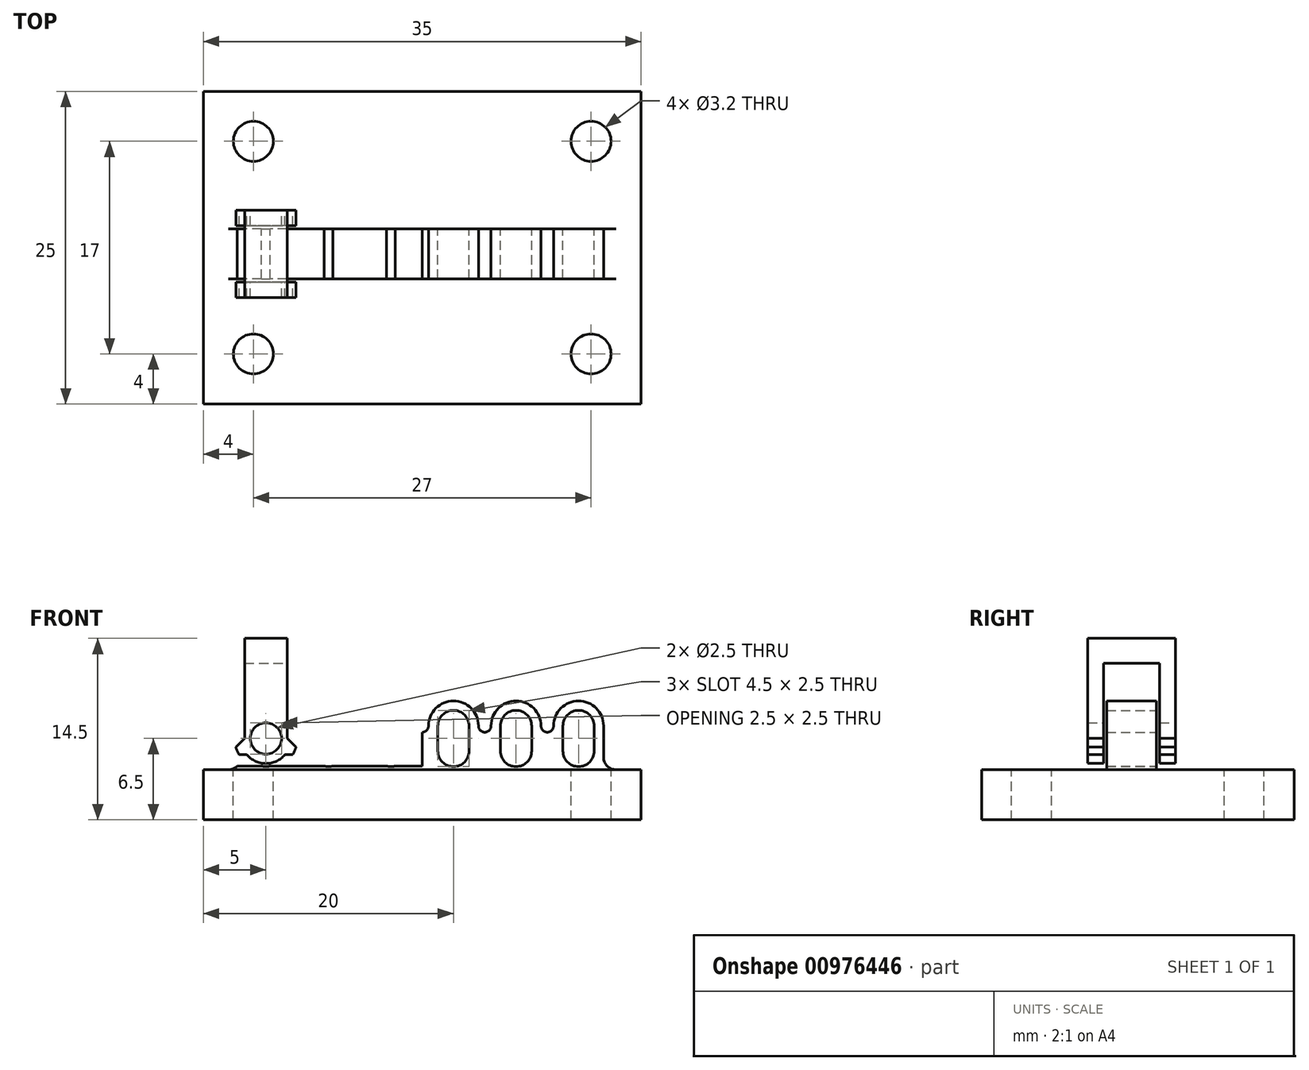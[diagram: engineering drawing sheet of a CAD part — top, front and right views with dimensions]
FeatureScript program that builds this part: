
annotation { "Feature Type Name" : "Feature", "Feature Type Description" : "" }
export const myFeature = defineFeature(function(context is Context, id is Id, definition is map)
    precondition{}
    {
        {
            var Q0;
            Q0=qCreatedBy(makeId("Front.planeOp"),FACE);
            var sketch = newSketch(context, id + "F0", { "sketchPlane" : qUnion([Q0])});
            skLineSegment(sketch, "E0.left", {"start": v(-1.25, 1) * mm, "end": v(-1.25, -1) * mm});
            skLineSegment(sketch, "E0.right", {"start": v(1.25, 1) * mm, "end": v(1.25, -1) * mm});
            skArc(sketch, "E1", {"start": v(1.25, 1) * mm, "mid": v(0, 2.25) * mm, "end": v(-1.25, 1) * mm});
            skArc(sketch, "E2", {"start": v(-1.25, -1) * mm, "mid": v(0, -2.25) * mm, "end": v(1.25, -1) * mm});
            skArc(sketch, "E3.1.0.0", {"start": v(3.75, -1) * mm, "mid": v(5, -2.25) * mm, "end": v(6.25, -1) * mm});
            skArc(sketch, "E3.1.0.1", {"start": v(6.25, 1) * mm, "mid": v(5, 2.25) * mm, "end": v(3.75, 1) * mm});
            skLineSegment(sketch, "E3.1.0.2", {"start": v(6.25, 1) * mm, "end": v(6.25, -1) * mm});
            skLineSegment(sketch, "E3.1.0.3", {"start": v(3.75, 1) * mm, "end": v(3.75, -1) * mm});
            skArc(sketch, "E3.2.0.0", {"start": v(8.75, -1) * mm, "mid": v(10, -2.25) * mm, "end": v(11.25, -1) * mm});
            skArc(sketch, "E3.2.0.1", {"start": v(11.25, 1) * mm, "mid": v(10, 2.25) * mm, "end": v(8.75, 1) * mm});
            skLineSegment(sketch, "E3.2.0.2", {"start": v(11.25, 1) * mm, "end": v(11.25, -1) * mm});
            skLineSegment(sketch, "E3.2.0.3", {"start": v(8.75, 1) * mm, "end": v(8.75, -1) * mm});
            skArc(sketch, "E3.3.0.0", {"start": v(13.75, -1) * mm, "mid": v(15, -2.25) * mm, "end": v(16.25, -1) * mm});
            skArc(sketch, "E3.3.0.1", {"start": v(16.25, 1) * mm, "mid": v(15, 2.25) * mm, "end": v(13.75, 1) * mm});
            skLineSegment(sketch, "E3.3.0.2", {"start": v(16.25, 1) * mm, "end": v(16.25, -1) * mm});
            skLineSegment(sketch, "E3.3.0.3", {"start": v(13.75, 1) * mm, "end": v(13.75, -1) * mm});
            skArc(sketch, "E3.4.0.0", {"start": v(18.75, -1) * mm, "mid": v(20, -2.25) * mm, "end": v(21.25, -1) * mm});
            skArc(sketch, "E3.4.0.1", {"start": v(21.25, 1) * mm, "mid": v(20, 2.25) * mm, "end": v(18.75, 1) * mm});
            skLineSegment(sketch, "E3.4.0.2", {"start": v(21.25, 1) * mm, "end": v(21.25, -1) * mm});
            skLineSegment(sketch, "E3.4.0.3", {"start": v(18.75, 1) * mm, "end": v(18.75, -1) * mm});
            skArc(sketch, "E3.5.0.0", {"start": v(23.75, -1) * mm, "mid": v(25, -2.25) * mm, "end": v(26.25, -1) * mm});
            skArc(sketch, "E3.5.0.1", {"start": v(26.25, 1) * mm, "mid": v(25, 2.25) * mm, "end": v(23.75, 1) * mm});
            skLineSegment(sketch, "E3.5.0.2", {"start": v(26.25, 1) * mm, "end": v(26.25, -1) * mm});
            skLineSegment(sketch, "E3.5.0.3", {"start": v(23.75, 1) * mm, "end": v(23.75, -1) * mm});
            skLineSegment(sketch, "E3.direction1", {"start": v(-1.25, -1) * mm, "end": v(3.75, -1) * mm, "construction": true});
            skLineSegment(sketch, "E4", {"start": v(-5, -6.5) * mm, "end": v(30, -6.5) * mm});
            skLineSegment(sketch, "E5", {"start": v(30, -6.5) * mm, "end": v(30, -2.5) * mm});
            skLineSegment(sketch, "E6", {"start": v(30, -2.5) * mm, "end": v(28, -2.5) * mm});
            skArc(sketch, "E7", {"start": v(27, -1.5) * mm, "mid": v(27.3, -2.2) * mm, "end": v(28, -2.5) * mm});
            skLineSegment(sketch, "E8", {"start": v(27, -1.5) * mm, "end": v(27, 1) * mm});
            skArc(sketch, "E9", {"start": v(27, 1) * mm, "mid": v(25, 3) * mm, "end": v(23, 1) * mm});
            skArc(sketch, "E10", {"start": v(22, 1) * mm, "mid": v(20, 3) * mm, "end": v(18, 1) * mm});
            skArc(sketch, "E11", {"start": v(17, 1) * mm, "mid": v(15, 3) * mm, "end": v(13, 1) * mm});
            skArc(sketch, "E12", {"start": v(12, 1) * mm, "mid": v(10, 3) * mm, "end": v(8, 1) * mm});
            skArc(sketch, "E13", {"start": v(7, 1) * mm, "mid": v(5, 3) * mm, "end": v(3, 1) * mm});
            skArc(sketch, "E14", {"start": v(2, 1) * mm, "mid": v(0, 3) * mm, "end": v(-2, 1) * mm});
            skLineSegment(sketch, "E15", {"start": v(-2, 1) * mm, "end": v(-2, -1.5) * mm});
            skArc(sketch, "E16", {"start": v(-3, -2.5) * mm, "mid": v(-2.3, -2.2) * mm, "end": v(-2, -1.5) * mm});
            skLineSegment(sketch, "E17", {"start": v(-3, -2.5) * mm, "end": v(-5, -2.5) * mm});
            skLineSegment(sketch, "E18", {"start": v(-5, -2.5) * mm, "end": v(-5, -6.5) * mm});
            skArc(sketch, "E19", {"start": v(2, 1) * mm, "mid": v(2.5, 0.5) * mm, "end": v(3, 1) * mm});
            skArc(sketch, "E20", {"start": v(7, 1) * mm, "mid": v(7.5, 0.5) * mm, "end": v(8, 1) * mm});
            skArc(sketch, "E21", {"start": v(12, 1) * mm, "mid": v(12.5, 0.5) * mm, "end": v(13, 1) * mm});
            skArc(sketch, "E22", {"start": v(17, 1) * mm, "mid": v(17.5, 0.5) * mm, "end": v(18, 1) * mm});
            skArc(sketch, "E23", {"start": v(22, 1) * mm, "mid": v(22.5, 0.5) * mm, "end": v(23, 1) * mm});
            skSolve(sketch);
        }
        {
            var Q0;
            Q0 = qSketchRegion(id + "F0", true);
            extrude(context, id + "F1", {"entities" : qUnion([Q0]), "endBound" : BoundingType.SYMMETRIC, "depth" : 4 * mm, "offsetDistance" : 25 * mm});
        }
        {
            var Q0;
            Q0=makeQuery(id+"F1.opExtrude","CAP_FACE",FACE,{"disambiguationData":[OSD([sQuery(id+"F0.wireOp",EDGE,"E0.left"),sQuery(id+"F0.wireOp",EDGE,"E0.right"),sQuery(id+"F0.wireOp",EDGE,"E1"),sQuery(id+"F0.wireOp",EDGE,"E2"),sQuery(id+"F0.wireOp",EDGE,"E3.1.0.0"),sQuery(id+"F0.wireOp",EDGE,"E3.1.0.1"),sQuery(id+"F0.wireOp",EDGE,"E3.1.0.2"),sQuery(id+"F0.wireOp",EDGE,"E3.1.0.3"),sQuery(id+"F0.wireOp",EDGE,"E3.2.0.0"),sQuery(id+"F0.wireOp",EDGE,"E3.2.0.1"),sQuery(id+"F0.wireOp",EDGE,"E3.2.0.2"),sQuery(id+"F0.wireOp",EDGE,"E3.2.0.3"),sQuery(id+"F0.wireOp",EDGE,"E3.3.0.0"),sQuery(id+"F0.wireOp",EDGE,"E3.3.0.1"),sQuery(id+"F0.wireOp",EDGE,"E3.3.0.2"),sQuery(id+"F0.wireOp",EDGE,"E3.3.0.3"),sQuery(id+"F0.wireOp",EDGE,"E3.4.0.0"),sQuery(id+"F0.wireOp",EDGE,"E3.4.0.1"),sQuery(id+"F0.wireOp",EDGE,"E3.4.0.2"),sQuery(id+"F0.wireOp",EDGE,"E3.4.0.3"),sQuery(id+"F0.wireOp",EDGE,"E3.5.0.0"),sQuery(id+"F0.wireOp",EDGE,"E3.5.0.1"),sQuery(id+"F0.wireOp",EDGE,"E3.5.0.2"),sQuery(id+"F0.wireOp",EDGE,"E3.5.0.3"),sQuery(id+"F0.wireOp",EDGE,"E4"),sQuery(id+"F0.wireOp",EDGE,"E5"),sQuery(id+"F0.wireOp",EDGE,"E6"),sQuery(id+"F0.wireOp",EDGE,"E7"),sQuery(id+"F0.wireOp",EDGE,"E8"),sQuery(id+"F0.wireOp",EDGE,"E9"),sQuery(id+"F0.wireOp",EDGE,"E10"),sQuery(id+"F0.wireOp",EDGE,"E11"),sQuery(id+"F0.wireOp",EDGE,"E12"),sQuery(id+"F0.wireOp",EDGE,"E13"),sQuery(id+"F0.wireOp",EDGE,"E14"),sQuery(id+"F0.wireOp",EDGE,"E15"),sQuery(id+"F0.wireOp",EDGE,"E16"),sQuery(id+"F0.wireOp",EDGE,"E17"),sQuery(id+"F0.wireOp",EDGE,"E18"),sQuery(id+"F0.wireOp",EDGE,"E19"),sQuery(id+"F0.wireOp",EDGE,"E20"),sQuery(id+"F0.wireOp",EDGE,"E21"),sQuery(id+"F0.wireOp",EDGE,"E22"),sQuery(id+"F0.wireOp",EDGE,"E23")])],"isStart":false});
            var sketch = newSketch(context, id + "F2", { "sketchPlane" : qUnion([Q0])});
            skLineSegment(sketch, "E24.bottom", {"start": v(-5, -6.5) * mm, "end": v(30, -6.5) * mm});
            skLineSegment(sketch, "E24.top", {"start": v(-5, -2.5) * mm, "end": v(30, -2.5) * mm});
            skLineSegment(sketch, "E24.left", {"start": v(-5, -6.5) * mm, "end": v(-5, -2.5) * mm});
            skLineSegment(sketch, "E24.right", {"start": v(30, -6.5) * mm, "end": v(30, -2.5) * mm});
            skSolve(sketch);
        }
        {
            var Q0;
            Q0 = qSketchRegion(id + "F2", true);
            extrude(context, id + "F3", {"entities" : qUnion([Q0]), "operationType" : NewBodyOperationType.ADD, "depth" : 10 * mm, "offsetDistance" : 25 * mm, "hasSecondDirection" : true, "secondDirectionOppositeDirection" : true, "secondDirectionDepth" : 15 * mm});
        }
        {
            var Q0;
            Q0=qCreatedBy(makeId("Top.planeOp"),FACE);
            var sketch = newSketch(context, id + "F4", { "sketchPlane" : qUnion([Q0])});
            skCircle(sketch, "E25", {"center": v(-1, 9) * mm, "radius": 1.6 * mm});
            skCircle(sketch, "E26", {"center": v(26, 9) * mm, "radius": 1.6 * mm});
            skCircle(sketch, "E27", {"center": v(26, -8) * mm, "radius": 1.6 * mm});
            skCircle(sketch, "E28", {"center": v(-1, -8) * mm, "radius": 1.6 * mm});
            skLineSegment(sketch, "E29.bottom", {"start": v(-1, 9) * mm, "end": v(26, 9) * mm, "construction": true});
            skLineSegment(sketch, "E29.top", {"start": v(-1, -8) * mm, "end": v(26, -8) * mm, "construction": true});
            skLineSegment(sketch, "E29.left", {"start": v(-1, 9) * mm, "end": v(-1, -8) * mm, "construction": true});
            skLineSegment(sketch, "E29.right", {"start": v(26, 9) * mm, "end": v(26, -8) * mm, "construction": true});
            skSolve(sketch);
        }
        {
            var Q0;
            Q0 = qSketchRegion(id + "F4", true);
            var Q1;
            Q1=makeQuery(id+"F3.boolean.opBoolean","MERGE",FACE,{"derivedFrom":[makeQuery(id+"F1.opExtrude","SWEPT_FACE",FACE,{"disambiguationData":[OSD([sQuery(id+"F0.wireOp",EDGE,"E4")])]}),makeQuery(id+"F3.opExtrude","SWEPT_FACE",FACE,{"disambiguationData":[OSD([sQuery(id+"F2.wireOp",EDGE,"E24.bottom")])]})]});
            extrude(context, id + "F5", {"entities" : qUnion([Q0]), "operationType" : NewBodyOperationType.REMOVE, "endBound" : BoundingType.UP_TO_SURFACE, "oppositeDirection" : true, "depth" : 25 * mm, "endBoundEntityFace" : qUnion([Q1]), "offsetDistance" : 25 * mm});
        }
        {
            var Q0;
            Q0=qCreatedBy(makeId("Front.planeOp"),FACE);
            var sketch = newSketch(context, id + "F6", { "sketchPlane" : qUnion([Q0])});
            skCircle(sketch, "E30", {"center": v(0, 0) * mm, "radius": 1.25 * mm});
            skArc(sketch, "E31", {"start": v(-1.52, -1.3) * mm, "mid": v(0, -2) * mm, "end": v(1.52, -1.3) * mm});
            skArc(sketch, "E32", {"start": v(2.14, -1.3) * mm, "mid": v(2.29, -1) * mm, "end": v(2.4, -0.7) * mm});
            skArc(sketch, "E33", {"start": v(-2.14, -1.3) * mm, "mid": v(-2.29, -1) * mm, "end": v(-2.4, -0.7) * mm});
            skLineSegment(sketch, "E34", {"start": v(-2.14, -1.3) * mm, "end": v(-1.52, -1.3) * mm});
            skLineSegment(sketch, "E35", {"start": v(1.52, -1.3) * mm, "end": v(2.14, -1.3) * mm});
            skLineSegment(sketch, "E36", {"start": v(2.4, -0.7) * mm, "end": v(1.7, 0) * mm});
            skLineSegment(sketch, "E37", {"start": v(1.7, 0) * mm, "end": v(1.7, 8) * mm});
            skLineSegment(sketch, "E38", {"start": v(1.7, 8) * mm, "end": v(-1.7, 8) * mm});
            skLineSegment(sketch, "E39", {"start": v(-1.7, 8) * mm, "end": v(-1.7, 0) * mm});
            skLineSegment(sketch, "E40", {"start": v(-1.7, 0) * mm, "end": v(-2.4, -0.7) * mm});
            skSolve(sketch);
        }
        {
            var Q0;
            Q0 = qSketchRegion(id + "F6", true);
            extrude(context, id + "F7", {"entities" : qUnion([Q0]), "endBound" : BoundingType.SYMMETRIC, "depth" : 7 * mm, "offsetDistance" : 25 * mm, "hasSecondDirection" : true, "secondDirectionOppositeDirection" : true, "secondDirectionDepth" : 5 * mm});
        }
        {
            var Q0;
            Q0=qCreatedBy(makeId("Right.planeOp"),FACE);
            var sketch = newSketch(context, id + "F8", { "sketchPlane" : qUnion([Q0])});
            skLineSegment(sketch, "E41.bottom", {"start": v(2.25, -2.2) * mm, "end": v(-2.25, -2.2) * mm});
            skLineSegment(sketch, "E41.top", {"start": v(2.25, 6) * mm, "end": v(-2.25, 6) * mm});
            skLineSegment(sketch, "E41.left", {"start": v(2.25, -2.2) * mm, "end": v(2.25, 6) * mm});
            skLineSegment(sketch, "E41.right", {"start": v(-2.25, -2.2) * mm, "end": v(-2.25, 6) * mm});
            skSolve(sketch);
        }
        {
            var Q0;
            Q0 = qSketchRegion(id + "F8", true);
            extrude(context, id + "F9", {"entities" : qUnion([Q0]), "operationType" : NewBodyOperationType.REMOVE, "endBound" : BoundingType.SYMMETRIC, "oppositeDirection" : true, "depth" : 25 * mm, "offsetDistance" : 25 * mm});
        }
    });
